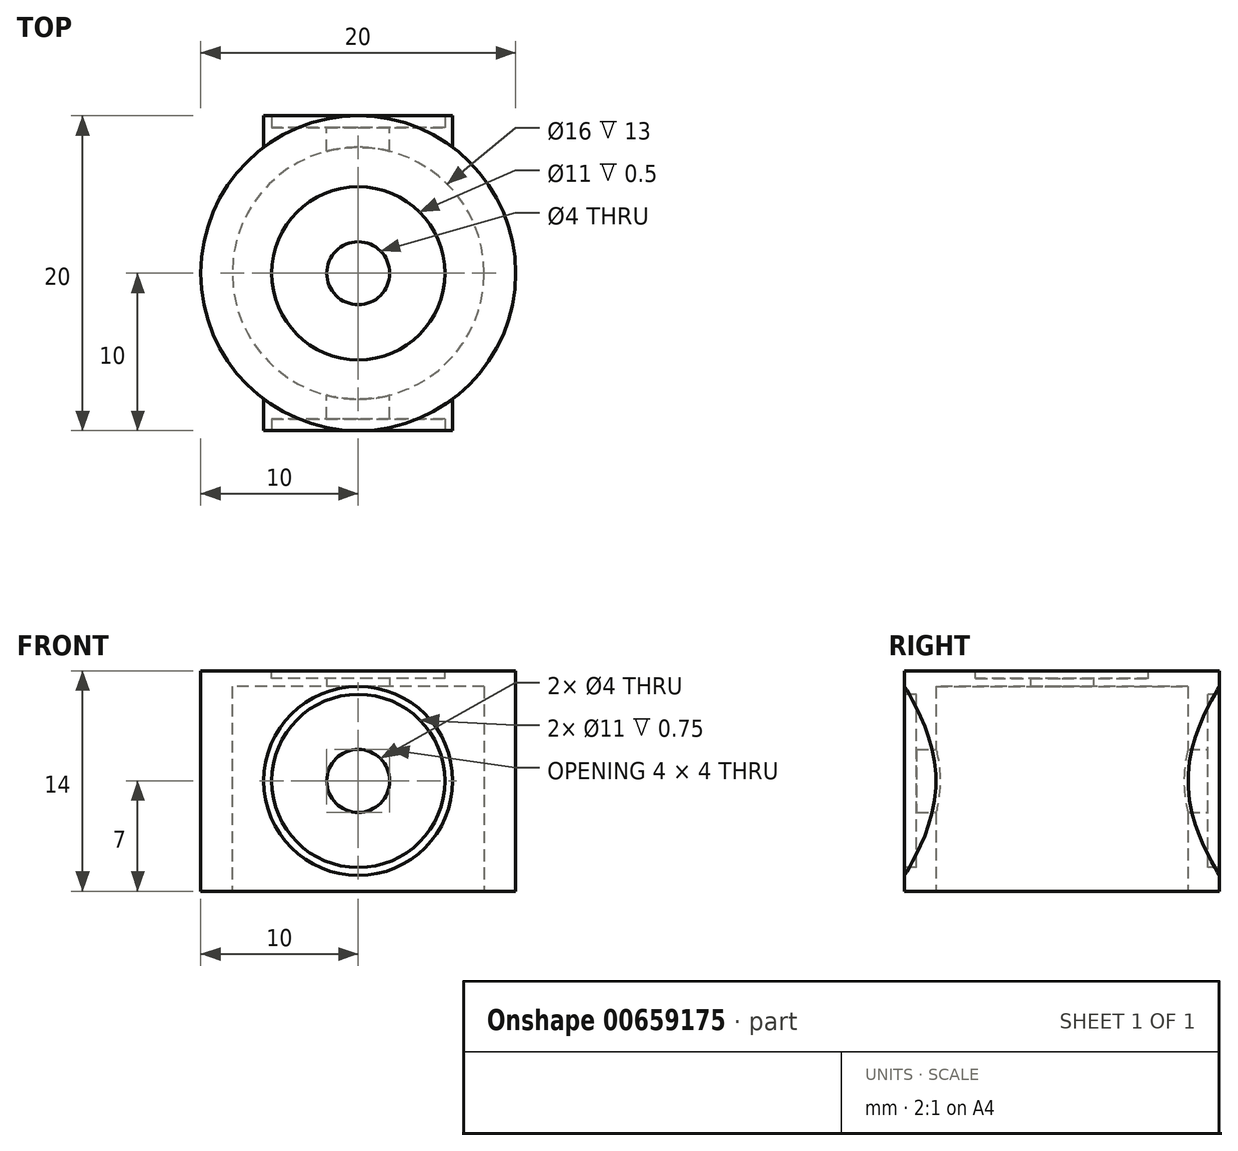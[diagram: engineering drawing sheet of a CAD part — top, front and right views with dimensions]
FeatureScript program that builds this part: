
annotation { "Feature Type Name" : "Feature", "Feature Type Description" : "" }
export const myFeature = defineFeature(function(context is Context, id is Id, definition is map)
    precondition{}
    {
        {
            var Q0;
            Q0=qCreatedBy(makeId("Top.planeOp"),FACE);
            var sketch = newSketch(context, id + "F0", { "sketchPlane" : qUnion([Q0])});
            skCircle(sketch, "E0", {"center": v(0, 0) * mm, "radius": 10 * mm});
            skSolve(sketch);
        }
        {
            var Q0;
            Q0 = qSketchRegion(id + "F0", true);
            extrude(context, id + "F1", {"entities" : qUnion([Q0]), "depth" : 14 * mm, "offsetDistance" : 25 * mm});
        }
        {
            var Q0;
            Q0=qCreatedBy(makeId("Front.planeOp"),FACE);
            var sketch = newSketch(context, id + "F2", { "sketchPlane" : qUnion([Q0])});
            skCircle(sketch, "E1", {"center": v(0, 7) * mm, "radius": 6 * mm});
            skSolve(sketch);
        }
        {
            var Q0;
            Q0 = qSketchRegion(id + "F2", true);
            extrude(context, id + "F3", {"entities" : qUnion([Q0]), "operationType" : NewBodyOperationType.ADD, "endBound" : BoundingType.SYMMETRIC, "depth" : 20 * mm, "offsetDistance" : 25 * mm});
        }
        {
            var Q0;
            Q0=qCreatedBy(makeId("Front.planeOp"),FACE);
            var sketch = newSketch(context, id + "F4", { "sketchPlane" : qUnion([Q0])});
            skCircle(sketch, "E2", {"center": v(0, 7) * mm, "radius": 5.5 * mm});
            skSolve(sketch);
        }
        {
            var Q0;
            Q0 = qSketchRegion(id + "F4", true);
            extrude(context, id + "F5", {"entities" : qUnion([Q0]), "operationType" : NewBodyOperationType.REMOVE, "endBound" : BoundingType.SYMMETRIC, "oppositeDirection" : true, "depth" : 25 * mm, "offsetDistance" : 25 * mm});
        }
        {
            var Q0;
            Q0 = qSketchRegion(id + "F4", true);
            extrude(context, id + "F6", {"entities" : qUnion([Q0]), "operationType" : NewBodyOperationType.ADD, "endBound" : BoundingType.SYMMETRIC, "depth" : 18.5 * mm, "offsetDistance" : 25 * mm});
        }
        {
            var Q0;
            Q0=qCreatedBy(makeId("Front.planeOp"),FACE);
            var sketch = newSketch(context, id + "F7", { "sketchPlane" : qUnion([Q0])});
            skCircle(sketch, "E3", {"center": v(0, 7) * mm, "radius": 2 * mm});
            skSolve(sketch);
        }
        {
            var Q0;
            Q0 = qSketchRegion(id + "F7", true);
            extrude(context, id + "F8", {"entities" : qUnion([Q0]), "operationType" : NewBodyOperationType.REMOVE, "endBound" : BoundingType.SYMMETRIC, "depth" : 25 * mm, "offsetDistance" : 25 * mm});
        }
        {
            var Q0;
            Q0=qCreatedBy(makeId("Top.planeOp"),FACE);
            var sketch = newSketch(context, id + "F9", { "sketchPlane" : qUnion([Q0])});
            skCircle(sketch, "E4", {"center": v(0, 0) * mm, "radius": 8 * mm});
            skSolve(sketch);
        }
        {
            var Q0;
            Q0 = qSketchRegion(id + "F9", true);
            extrude(context, id + "F10", {"entities" : qUnion([Q0]), "operationType" : NewBodyOperationType.REMOVE, "depth" : 13 * mm, "offsetDistance" : 25 * mm});
        }
        {
            var Q0;
            Q0=makeQuery(id+"F1.opExtrude","CAP_FACE",FACE,{"disambiguationData":[OSD([sQuery(id+"F0.wireOp",EDGE,"E0")])],"isStart":false});
            var sketch = newSketch(context, id + "F11", { "sketchPlane" : qUnion([Q0])});
            skCircle(sketch, "E5", {"center": v(0, 0) * mm, "radius": 5.5 * mm});
            skSolve(sketch);
        }
        {
            var Q0;
            Q0 = qSketchRegion(id + "F11", true);
            extrude(context, id + "F12", {"entities" : qUnion([Q0]), "operationType" : NewBodyOperationType.REMOVE, "oppositeDirection" : true, "depth" : .5 * mm, "offsetDistance" : 25 * mm});
        }
        {
            var Q0;
            Q0=qCreatedBy(makeId("Top.planeOp"),FACE);
            var sketch = newSketch(context, id + "F13", { "sketchPlane" : qUnion([Q0])});
            skCircle(sketch, "E6", {"center": v(0, 0) * mm, "radius": 2 * mm});
            skSolve(sketch);
        }
        {
            var Q0;
            Q0 = qSketchRegion(id + "F13", true);
            extrude(context, id + "F14", {"entities" : qUnion([Q0]), "operationType" : NewBodyOperationType.REMOVE, "depth" : 25 * mm, "offsetDistance" : 25 * mm});
        }
    });
